# Revit family: bfs-20_60sldc2_60Hz
name_source: partatom
category: 機械設備
units: mm (PartAtom-declared; Revit-internal decimal feet)

## family parameters
OmniClass タイトル = Centrifugal Fans
OmniClass 番号 = 23.75.35.17.27
パーツ タイプ = 割り込み
ロード時にボイドで切り取り = いいえ
丸型コネクタ寸法 = 直径を使用
作業面ベース = いいえ
共有 = いいえ
常に垂直 = はい
部屋計算ポイント = はい

## types (3) — shared parameters
Clearance Left = 450  [stored 1.47638 ft]
IfcExportAs = IfcFanType
IfcExportType = CENTRIFUGALFORWARDCURVED
MID静圧 = 0.0 Pa
MID風量 = 0.0 m³/h
OmniClassCode = 23-33 31 19 13 15
URL = https://www.mitsubishielectric.co.jp
Uniclass2015Code = Pr_65_67_29_12
Uniclass2015Title = Centrifugal fans
Uniclass2015Version = Systems v1.9
サービススペース = はい
ファンの種類 = 多翼形
仕様書バージョン = Version1.0
企業コード = 108420
分類コード = 50052502100020
周波数 = 60 Hz
呼称 = 消音ボックス付送風機
実風量 = 0.0 m³/h
形名 = BFS-SLDC : BFS-20SLDC
本体マテリアル = 溶融亜鉛めっき鋼板
極数 = 2
法定耐用年数 = 15
盤工事区分 = 電気工事
相 = 1
積算_科目 = 2 換気設備
製品リリース年月 = 2022年6月1日
製品出荷対象 = 国内
製造元 = 三菱電機株式会社
設置方法 = 天吊
説明 = ストレートシロッコファン（２４時間換気機能付）
負荷分類 = 3_ファン類
運転質量 = 0.00 kg
電圧 = 100 V
zero-valued in all types: Clearance Back, Clearance Bottom, Clearance Front, Clearance Right, Clearance Top

## per-type parameters (varying)
| type | Depth | Height | M | MAX静圧 | MAX風量 | MIN静圧 | MIN風量 | Width | ダクト径 | 価格 | 天吊金具ピッチ奥行 | 天吊金具ピッチ幅 | 極 | 消費電力 | 番手 | 製品質量 | 質量 | 電動機出力 | 騒音レベル(dB(A)) | 騒音レベル(dB(A))_側面 | 騒音レベル(dB(A))_吐出 | 騒音レベル(dB(A))_吸込 |
| BFS-20SLDC2 | 335  [stored 1.09908 ft] | 225  [stored 0.738189 ft] | 60  [stored 0.19685 ft] | 50.0 Pa | 200.0 m³/h | 12.5 Pa | 100.0 m³/h | 223  [stored 0.731627 ft] | 100 mm | 81000 $ | 300  [stored 0.984252 ft] | 299  [stored 0.980971 ft] | 8 | 17 W | #1 | 6.00 kg | 7.20 kg | 15 W | 38 | 22 | 38 | 30.5 |
| BFS-40SLDC2 | 388  [stored 1.27297 ft] | 255  [stored 0.836614 ft] | 70  [stored 0.229659 ft] | 69.0 Pa | 400.0 m³/h | 11.0 Pa | 160.0 m³/h | 305  [stored 1.00066 ft] | 150 mm | 115000 $ | 353  [stored 1.15814 ft] | 381  [stored 1.25 ft] | 8 | 38 W | #1 1/4 | 9.00 kg | 10.80 kg | 35 W | 44 | 24 | 44 | 34.5 |
| BFS-60SLDC2 | 488  [stored 1.60105 ft] | 305  [stored 1.00066 ft] | 85  [stored 0.278871 ft] | 120.0 Pa | 600.0 m³/h | 19.0 Pa | 240.0 m³/h | 373  [stored 1.22375 ft] | 200 mm | 169000 $ | 453  [stored 1.48622 ft] | 449  [stored 1.4731 ft] | 10 | 60 W | #1 1/4 | 13.00 kg | 15.60 kg | 50 W | 47 | 23 | 47 | 34 |

note: column(s) folded — value = type name in every type: モデル

note: [stored X ft] marks values corroborated as IEEE doubles in the binary element streams (Revit-internal decimal feet)
